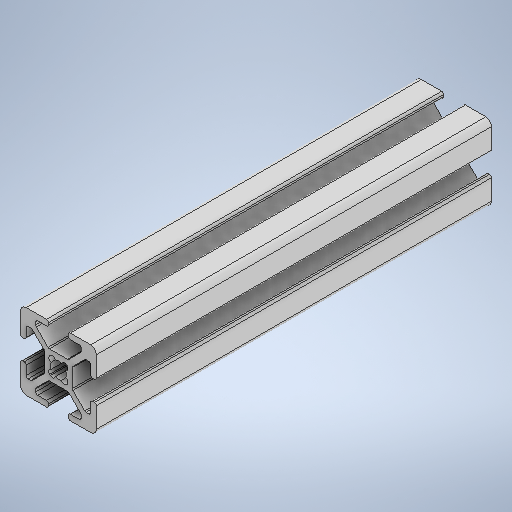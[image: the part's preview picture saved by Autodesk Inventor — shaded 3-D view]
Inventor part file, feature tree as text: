
AUTODESK INVENTOR PART (.ipt)
format: ipt  version: 2025 (Build 290162000, 162)  size: 373,760 bytes
history: native  units: mm
features: extrude x1, sketch x1
ambient origin geometry x8: Origin, YZ Plane, XZ Plane, XY Plane, X Axis, Y Axis, Z Axis, Center Point
bodies: Solid1 (feature_tree)
feature tree (2):
  extrude  "Extrusion1"  Depth=104.025mm
  sketch  "Sketch1"  dims[d0=104.025mm d1=0.0mm d2=1.0mm d3=1.0mm d4=1.0mm d5=0.15mm d6=0.25mm d7=0.375mm d8=14.3117mm d9=0.75mm d10=20.594885mm d11=0.0625mm d12=0.75mm d13=0.375mm]
